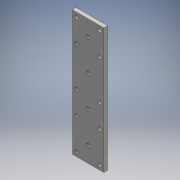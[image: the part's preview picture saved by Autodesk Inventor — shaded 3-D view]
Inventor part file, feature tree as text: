
AUTODESK INVENTOR PART (.ipt)
format: ipt  version: 2016 (Build 200138000, 138)  size: 151,552 bytes
history: native  units: mm
features: extrude x1, sketch x1
ambient origin geometry x8: Origin, YZ Plane, XZ Plane, XY Plane, X Axis, Y Axis, Z Axis, Center Point
bodies: Body1 (feature_tree)
feature tree (2):
  extrude  "Extrusion4"  Depth=6.39mm
  sketch  "Sketch1"  dims[d1=42.8241mm d2=33.8085mm d4=6.35mm d11=44.8241mm d12=6.35mm d13=6.35mm d14=6.35mm d15=54.0936mm d16=54.0936mm d17=54.0936mm d18=40.5702mm d19=42.5702mm d20=39.21786mm d21=41.21786mm d22=38.3163mm d23=40.3163mm d31=27.41205mm d32=27.41205mm d33=27.41205mm d34=27.41205mm d37=6.35mm d38=7.5mm d39=7.5mm d40=6.35mm d41=7.5mm d50=6.35mm d51=7.5mm d54=6.39mm d55=0.0mm]
